# Revit family: Mounted_Storage_&_Accessories-Teknion-ROCF_Overhead_Cabinet_Solid_Flipper_Doors-R2019
name_source: partatom
category: Furniture
units: mm (PartAtom-declared; Revit-internal decimal feet)

## family parameters
Always vertical = Yes
Cut with Voids When Loaded = No
OmniClass Number = 23.40.20.00
OmniClass Title = General Furniture and Specialties
Room Calculation Point = No
Shared = Yes
Work Plane-Based = No

## types (2) — shared parameters
Assembly Code = E2020200
Manufacturer = Teknion
Manufacturer Fax = 416.661.4586
Part Number = ROCF
Product Documentation Link = https://www.teknion.com
Product Line = Expansion Desking
Product Page URL = https://www.teknion.com
Series = Expansion Desking
Sustainability Data = https://www.teknion.com
URL = www.teknion.com
Unit Weight URL = http://www.teknion.com
Warranty = http://www.teknion.com

## per-type parameters (varying)
| type | Column Void Cut Offset | Column-Mounted | Description | Insertion X Point Offset | Insertion Y Point Offset | Model | Wall-Mounted |
| Column-Mounted, 16" Depth | 21.793 " | Yes | Overhead Cabinet – Solid Flipper Door(s), Column-Mounted, 16" Depth | 1.16 " | 1.16 " | ROCFC16__ | No |
| Wall-Mounted, 16" Depth | 0.5 " | No | Overhead Cabinet – Solid Flipper Door(s), Wall-Mounted, 16" Depth | 0 " | 0.75 " | ROCFW16__ | Yes |

## geometry (parser evidence)
native form markers: Sweep x2
no freeform markers — native parametric forms only
